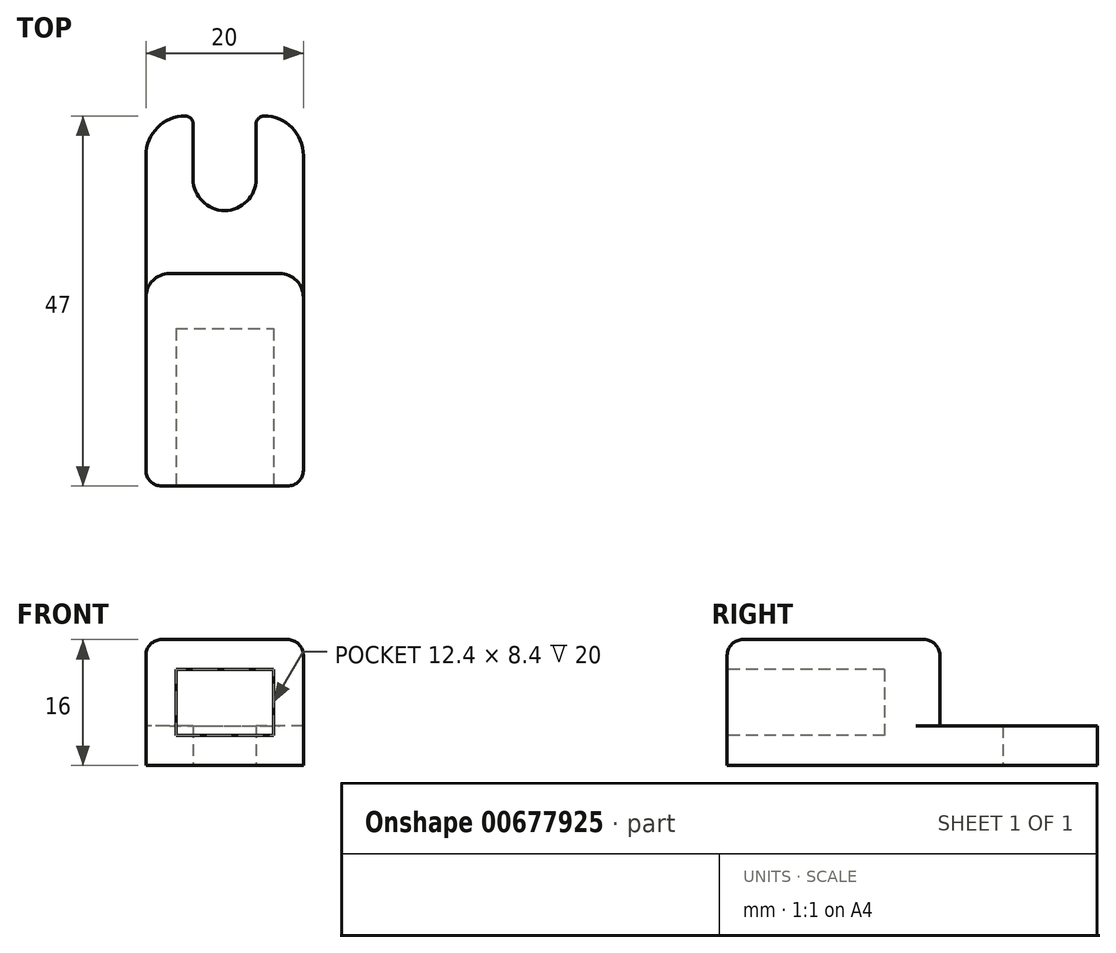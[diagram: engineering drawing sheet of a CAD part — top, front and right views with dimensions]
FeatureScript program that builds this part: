
annotation { "Feature Type Name" : "Feature", "Feature Type Description" : "" }
export const myFeature = defineFeature(function(context is Context, id is Id, definition is map)
    precondition{}
    {
        {
            var Q0;
            Q0=qCreatedBy(makeId("Top.planeOp"),FACE);
            var sketch = newSketch(context, id + "F0", { "sketchPlane" : qUnion([Q0])});
            skLineSegment(sketch, "E0", {"start": v(0, 0) * mm, "end": v(20, 0) * mm});
            skLineSegment(sketch, "E1", {"start": v(20, 0) * mm, "end": v(20, 42) * mm});
            skLineSegment(sketch, "E2", {"start": v(15, 47) * mm, "end": v(15, 47) * mm});
            skLineSegment(sketch, "E3", {"start": v(0, 42) * mm, "end": v(0, 0) * mm});
            skArc(sketch, "E4", {"start": v(6, 39) * mm, "mid": v(10, 35) * mm, "end": v(14, 39) * mm});
            skLineSegment(sketch, "E5", {"start": v(6, 46) * mm, "end": v(6, 39) * mm});
            skLineSegment(sketch, "E6", {"start": v(14, 46) * mm, "end": v(14, 39) * mm});
            skLineSegment(sketch, "E7.trimOffspring", {"start": v(5, 47) * mm, "end": v(5, 47) * mm});
            skPoint(sketch, "E8.visualSharp", {"position": v(0, 47) * mm});
            skArc(sketch, "E8.filletArc", {"start": v(5, 47) * mm, "mid": v(1.46, 45.54) * mm, "end": v(0, 42) * mm});
            skPoint(sketch, "E9.visualSharp", {"position": v(20, 47) * mm});
            skArc(sketch, "E9.filletArc", {"start": v(20, 42) * mm, "mid": v(18.54, 45.54) * mm, "end": v(15, 47) * mm});
            skPoint(sketch, "E10.visualSharp", {"position": v(6, 47) * mm});
            skArc(sketch, "E10.filletArc", {"start": v(6, 46) * mm, "mid": v(5.7, 46.7) * mm, "end": v(5, 47) * mm});
            skPoint(sketch, "E11.visualSharp", {"position": v(14, 47) * mm});
            skArc(sketch, "E11.filletArc", {"start": v(15, 47) * mm, "mid": v(14.3, 46.7) * mm, "end": v(14, 46) * mm});
            skSolve(sketch);
        }
        {
            var Q0;
            Q0=makeQuery(id+"F0.imprint","IMPRINT",FACE,{"disambiguationData":[TD([[makeQuery(id+"F0.imprint","IMPRINT",EDGE,{"derivedFrom":sQuery(id+"F0.wireOp",EDGE,"E0")}),1.0]])]});
            extrude(context, id + "F1", {"entities" : qUnion([Q0]), "depth" : 5 * mm, "offsetDistance" : 25 * mm});
        }
        {
            var Q0;
            Q0=makeQuery(id+"F1.opExtrude","CAP_FACE",FACE,{"disambiguationData":[OSD([sQuery(id+"F0.wireOp",EDGE,"E0"),sQuery(id+"F0.wireOp",EDGE,"E1"),sQuery(id+"F0.wireOp",EDGE,"E3"),sQuery(id+"F0.wireOp",EDGE,"E4"),sQuery(id+"F0.wireOp",EDGE,"E5"),sQuery(id+"F0.wireOp",EDGE,"E6"),sQuery(id+"F0.wireOp",EDGE,"E8.filletArc"),sQuery(id+"F0.wireOp",EDGE,"E9.filletArc"),sQuery(id+"F0.wireOp",EDGE,"E10.filletArc"),sQuery(id+"F0.wireOp",EDGE,"E11.filletArc")])],"isStart":false});
            var sketch = newSketch(context, id + "F2", { "sketchPlane" : qUnion([Q0])});
            skLineSegment(sketch, "E12", {"start": v(0, 0) * mm, "end": v(0, 24) * mm});
            skLineSegment(sketch, "E13", {"start": v(3, 27) * mm, "end": v(17, 27) * mm});
            skLineSegment(sketch, "E14", {"start": v(20, 24) * mm, "end": v(20, 0) * mm});
            skLineSegment(sketch, "E15", {"start": v(20, 0) * mm, "end": v(0, 0) * mm});
            skPoint(sketch, "E16.visualSharp", {"position": v(0, 27) * mm});
            skArc(sketch, "E16.filletArc", {"start": v(3, 27) * mm, "mid": v(0.88, 26.12) * mm, "end": v(0, 24) * mm});
            skPoint(sketch, "E17.visualSharp", {"position": v(20, 27) * mm});
            skArc(sketch, "E17.filletArc", {"start": v(20, 24) * mm, "mid": v(19.12, 26.12) * mm, "end": v(17, 27) * mm});
            skSolve(sketch);
        }
        {
            var Q0;
            Q0=makeQuery(id+"F2.imprint","IMPRINT",FACE,{"disambiguationData":[TD([[makeQuery(id+"F2.imprint","IMPRINT",EDGE,{"derivedFrom":sQuery(id+"F2.wireOp",EDGE,"E12")}),1.0]])]});
            extrude(context, id + "F3", {"entities" : qUnion([Q0]), "operationType" : NewBodyOperationType.ADD, "depth" : 11 * mm, "offsetDistance" : 25 * mm});
        }
        {
            var Q0;
            Q0=makeQuery(id+"F3.boolean.opBoolean","MERGE",FACE,{"derivedFrom":[makeQuery(id+"F1.opExtrude","SWEPT_FACE",FACE,{"disambiguationData":[OSD([sQuery(id+"F0.wireOp",EDGE,"E0")])]}),makeQuery(id+"F3.opExtrude","SWEPT_FACE",FACE,{"disambiguationData":[OSD([sQuery(id+"F2.wireOp",EDGE,"E15")])]})]});
            var sketch = newSketch(context, id + "F4", { "sketchPlane" : qUnion([Q0])});
            skLineSegment(sketch, "E18", {"start": v(3.8, 3.8) * mm, "end": v(16.2, 3.8) * mm});
            skLineSegment(sketch, "E19", {"start": v(16.2, 3.8) * mm, "end": v(16.2, 12.2) * mm});
            skLineSegment(sketch, "E20", {"start": v(16.2, 12.2) * mm, "end": v(3.8, 12.2) * mm});
            skLineSegment(sketch, "E21", {"start": v(3.8, 12.2) * mm, "end": v(3.8, 3.8) * mm});
            skSolve(sketch);
        }
        {
            var Q0;
            Q0=makeQuery(id+"F4.imprint","IMPRINT",FACE,{"disambiguationData":[TD([[makeQuery(id+"F4.imprint","IMPRINT",EDGE,{"derivedFrom":sQuery(id+"F4.wireOp",EDGE,"E18")}),1.0]])]});
            extrude(context, id + "F5", {"entities" : qUnion([Q0]), "operationType" : NewBodyOperationType.REMOVE, "oppositeDirection" : true, "depth" : 20 * mm, "offsetDistance" : 25 * mm});
        }
        {
            var Q0;
            Q0=makeQuery(id+"F3.boolean.opBoolean","MERGE",EDGE,{"derivedFrom":[makeQuery(id+"F1.opExtrude","SWEPT_EDGE",EDGE,{"disambiguationData":[OSD([sQuery(id+"F0.wireOp",EDGE,"E0"),sQuery(id+"F0.wireOp",EDGE,"E3")])]}),makeQuery(id+"F3.opExtrude","SWEPT_EDGE",EDGE,{"disambiguationData":[OSD([sQuery(id+"F2.wireOp",EDGE,"E12"),sQuery(id+"F2.wireOp",EDGE,"E15")])]})]});
            var Q1;
            Q1=makeQuery(id+"F3.boolean.opBoolean","MERGE",EDGE,{"derivedFrom":[makeQuery(id+"F1.opExtrude","SWEPT_EDGE",EDGE,{"disambiguationData":[OSD([sQuery(id+"F0.wireOp",EDGE,"E0"),sQuery(id+"F0.wireOp",EDGE,"E1")])]}),makeQuery(id+"F3.opExtrude","SWEPT_EDGE",EDGE,{"disambiguationData":[OSD([sQuery(id+"F2.wireOp",EDGE,"E14"),sQuery(id+"F2.wireOp",EDGE,"E15")])]})]});
            var Q2;
            Q2=makeQuery(id+"F3.opExtrude","CAP_EDGE",EDGE,{"disambiguationData":[OSD([sQuery(id+"F2.wireOp",EDGE,"E14")])],"isStart":false});
            var Q3;
            Q3=makeQuery(id+"F3.opExtrude","CAP_EDGE",EDGE,{"disambiguationData":[OSD([sQuery(id+"F2.wireOp",EDGE,"E15")])],"isStart":false});
            fillet(context, id + "F6", {"entities" : qUnion([Q0, Q1, Q2, Q3]), "radius" : 2 * mm, "tangentPropagation" : true, "allowEdgeOverflow" : false});
        }
    });
